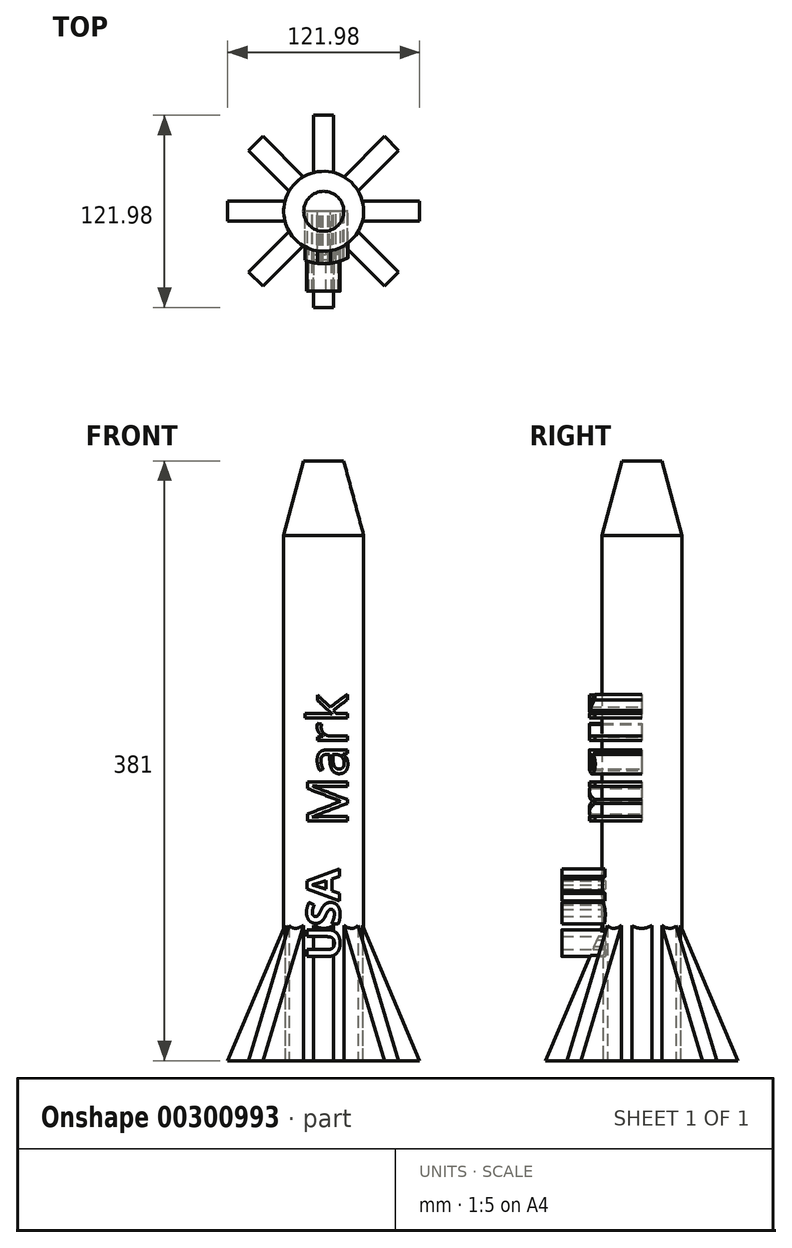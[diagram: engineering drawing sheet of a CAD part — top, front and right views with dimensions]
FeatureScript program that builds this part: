
annotation { "Feature Type Name" : "Feature", "Feature Type Description" : "" }
export const myFeature = defineFeature(function(context is Context, id is Id, definition is map)
    precondition{}
    {
        {
            var Q0;
            Q0=qCreatedBy(makeId("Top.planeOp"),FACE);
            var sketch = newSketch(context, id + "F0", { "sketchPlane" : qUnion([Q0])});
            skCircle(sketch, "E0", {"center": v(0, 0) * mm, "radius": 25.4 * mm});
            skSolve(sketch);
        }
        {
            var Q0;
            Q0 = qSketchRegion(id + "F0", true);
            extrude(context, id + "F1", {"entities" : qUnion([Q0]), "depth" : 381 * mm});
        }
        {
            var Q0;
            Q0=makeQuery(id+"F1.opExtrude","CAP_EDGE",EDGE,{"disambiguationData":[OSD([sQuery(id+"F0.wireOp",EDGE,"E0")])],"isStart":false});
            chamfer(context, id + "F2", {"entities" : qUnion([Q0]), "chamferType" : ChamferType.OFFSET_ANGLE, "width" : 12.7 * mm, "oppositeDirection" : false, "angle" : 75 * degree, "tangentPropagation" : true});
        }
        {
            var Q0;
            Q0=qCreatedBy(makeId("Front.planeOp"),FACE);
            var sketch = newSketch(context, id + "F3", { "sketchPlane" : qUnion([Q0])});
            skLineSegment(sketch, "E1", {"start": v(0, 0) * mm, "end": v(0, 144.02) * mm});
            skLineSegment(sketch, "E2", {"start": v(0, 144.02) * mm, "end": v(61, 0) * mm});
            skLineSegment(sketch, "E3", {"start": v(61, 0) * mm, "end": v(0, 0) * mm});
            skSolve(sketch);
        }
        {
            var Q0;
            Q0=makeQuery(id+"F3.imprint","IMPRINT",FACE,{"disambiguationData":[TD([[makeQuery(id+"F3.imprint","IMPRINT",EDGE,{"derivedFrom":sQuery(id+"F3.wireOp",EDGE,"E1")}),-1.0]])]});
            extrude(context, id + "F4", {"entities" : qUnion([Q0]), "operationType" : NewBodyOperationType.ADD, "endBound" : BoundingType.SYMMETRIC, "depth" : 12.7 * mm});
        }
        {
            var Q0;
            Q0=makeQuery(id+"F1.opExtrude","SWEPT_BODY",BODY,{"disambiguationData":[OSD([sQuery(id+"F0.wireOp",EDGE,"E0")])]});
            var Q1;
            Q1=makeQuery(id+"F1.opExtrude","SWEPT_FACE",FACE,{"disambiguationData":[OSD([sQuery(id+"F0.wireOp",EDGE,"E0")])]});
            circularPattern(context, id + "F5", {"entities" : qUnion([Q0]), "axis" : qUnion([Q1]), "angle" : 360 * degree, "instanceCount" : 8, "equalSpace" : true});
        }
        {
            var Q0;
            Q0=qCreatedBy(makeId("Front.planeOp"),FACE);
            var sketch = newSketch(context, id + "F6", { "sketchPlane" : qUnion([Q0])});
            skText(sketch, "E4", { "text": "Mark", "fontName": "OpenSans-Regular.ttf"});
            const initialGuessF6  = {"E4": [0.015, 0.14884, 0, 1, 0.02536]};
            skSetInitialGuess(sketch, initialGuessF6);
            skSolve(sketch);
        }
        {
            var Q0;
            Q0=qCreatedBy(makeId("Top.planeOp"),FACE);
            var sketch = newSketch(context, id + "F7", { "sketchPlane" : qUnion([Q0])});
            skCircle(sketch, "E5", {"center": v(0, 0) * mm, "radius": 33.27 * mm});
            skSolve(sketch);
        }
        {
            var Q0;
            Q0 = qSketchRegion(id + "F7", true);
            var Q1;
            Q1=sQuery(id+"F7.wireOp",EDGE,"E5");
            extrude(context, id + "F8", {"entities" : qUnion([Q0]), "bodyType" : ToolBodyType.SURFACE, "surfaceEntities" : qUnion([Q1]), "depth" : 25.4 * mm});
        }
        {
            var Q0;
            Q0 = qSketchRegion(id + "F6", true);
            var Q1;
            Q1=makeQuery(id+"F8.opExtrude","SWEPT_FACE",FACE,{"disambiguationData":[OSD([sQuery(id+"F7.wireOp",EDGE,"E5")])]});
            extrude(context, id + "F9", {"entities" : qUnion([Q0]), "endBound" : BoundingType.UP_TO_SURFACE, "endBoundEntityFace" : qUnion([Q1]), "depth" : 25.4 * mm});
        }
        {
            var Q0;
            Q0=makeQuery(id+"F8.opExtrude","SWEPT_BODY",BODY,{"disambiguationData":[OSD([sQuery(id+"F7.wireOp",EDGE,"E5")])]});
            deleteBodies(context, id + "F10", {"entities" : qUnion([Q0])});
        }
        {
            var Q0;
            Q0=qCreatedBy(makeId("Front.planeOp"),FACE);
            var sketch = newSketch(context, id + "F11", { "sketchPlane" : qUnion([Q0])});
            skText(sketch, "E6", { "text": "USA", "fontName": "OpenSans-Bold.ttf"});
            const initialGuessF11  = {"E6": [0.01014, 0.06368, 0, 1, 0.02091]};
            skSetInitialGuess(sketch, initialGuessF11);
            skSolve(sketch);
        }
        {
            var Q0;
            Q0 = qSketchRegion(id + "F11", true);
            extrude(context, id + "F12", {"entities" : qUnion([Q0]), "operationType" : NewBodyOperationType.ADD, "depth" : 50.8 * mm});
        }
    });
